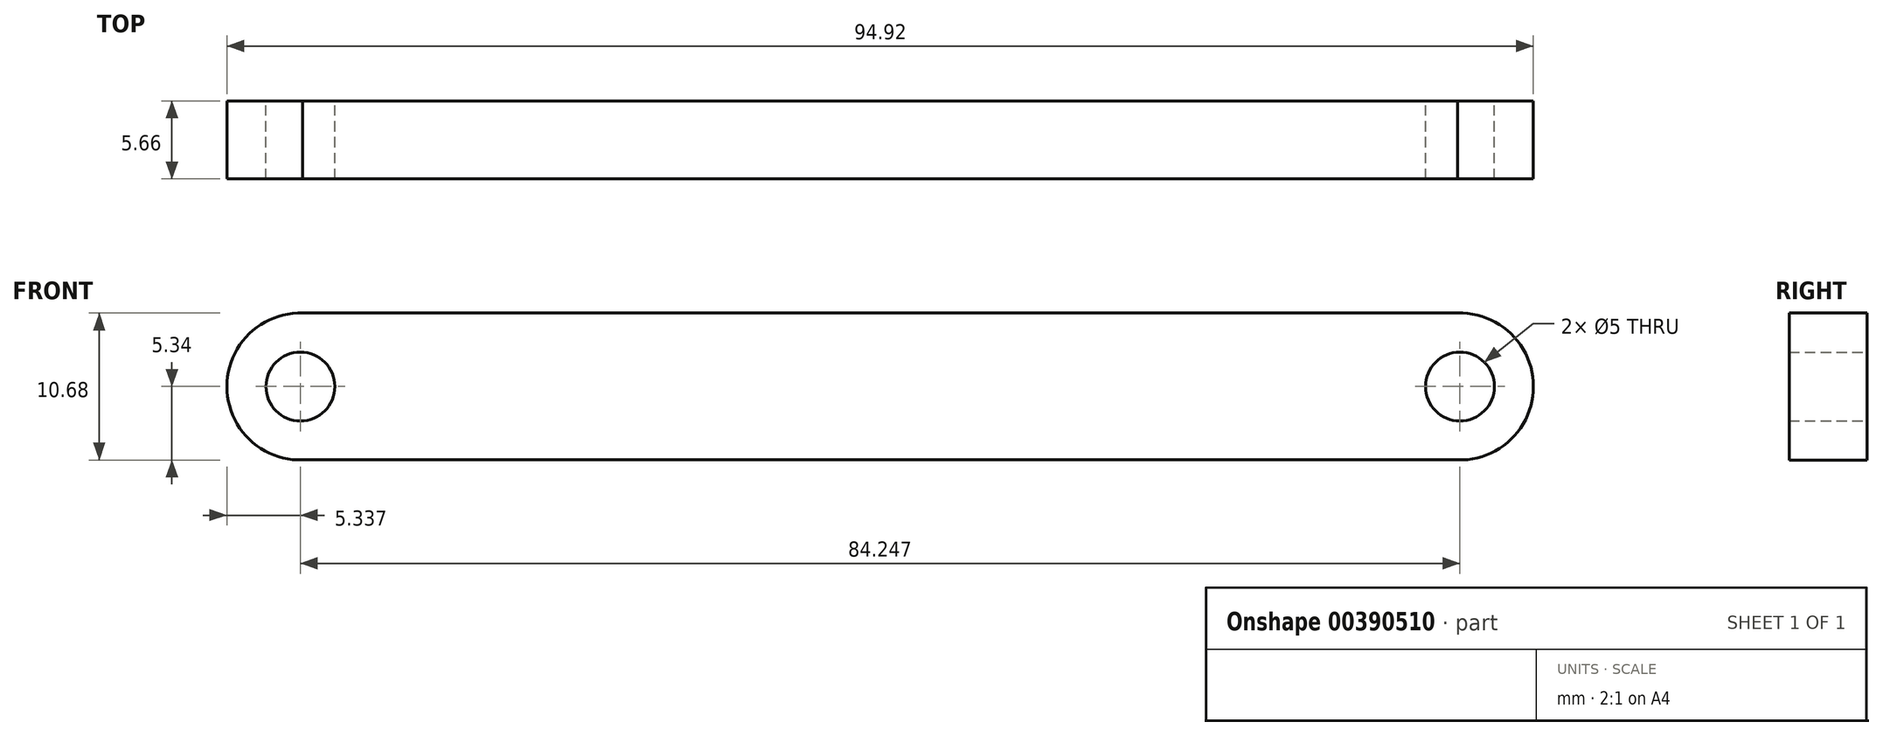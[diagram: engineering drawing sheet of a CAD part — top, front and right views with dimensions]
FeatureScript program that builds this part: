
annotation { "Feature Type Name" : "Feature", "Feature Type Description" : "" }
export const myFeature = defineFeature(function(context is Context, id is Id, definition is map)
    precondition{}
    {
        {
            var Q0;
            Q0=qCreatedBy(makeId("Front.planeOp"),FACE);
            var sketch = newSketch(context, id + "F0", { "sketchPlane" : qUnion([Q0])});
            skLineSegment(sketch, "E0.bottom", {"start": v(42.3, -5.33) * mm, "end": v(-42.3, -5.33) * mm});
            skLineSegment(sketch, "E0.top", {"start": v(42.3, 5.33) * mm, "end": v(-42.3, 5.33) * mm});
            skPoint(sketch, "E0.middle", {"position": v(0, 0) * mm});
            skCircle(sketch, "E1", {"center": v(-42.12, 0) * mm, "radius": 2.5 * mm});
            skCircle(sketch, "E2.MirrorC", {"center": v(42.12, 0) * mm, "radius": 2.5 * mm});
            skArc(sketch, "E3", {"start": v(-41.96, 5.33) * mm, "mid": v(-47.46, 0) * mm, "end": v(-41.96, -5.33) * mm});
            skArc(sketch, "E4.MirrorC", {"start": v(41.96, 5.33) * mm, "mid": v(47.46, 0) * mm, "end": v(41.96, -5.33) * mm});
            skSolve(sketch);
        }
        {
            var Q0;
            Q0=qSketchRegion(id+"F0",true);
            extrude(context, id + "F1", {"entities" : qUnion([Q0]), "depth" : 5.66 * mm});
        }
    });
